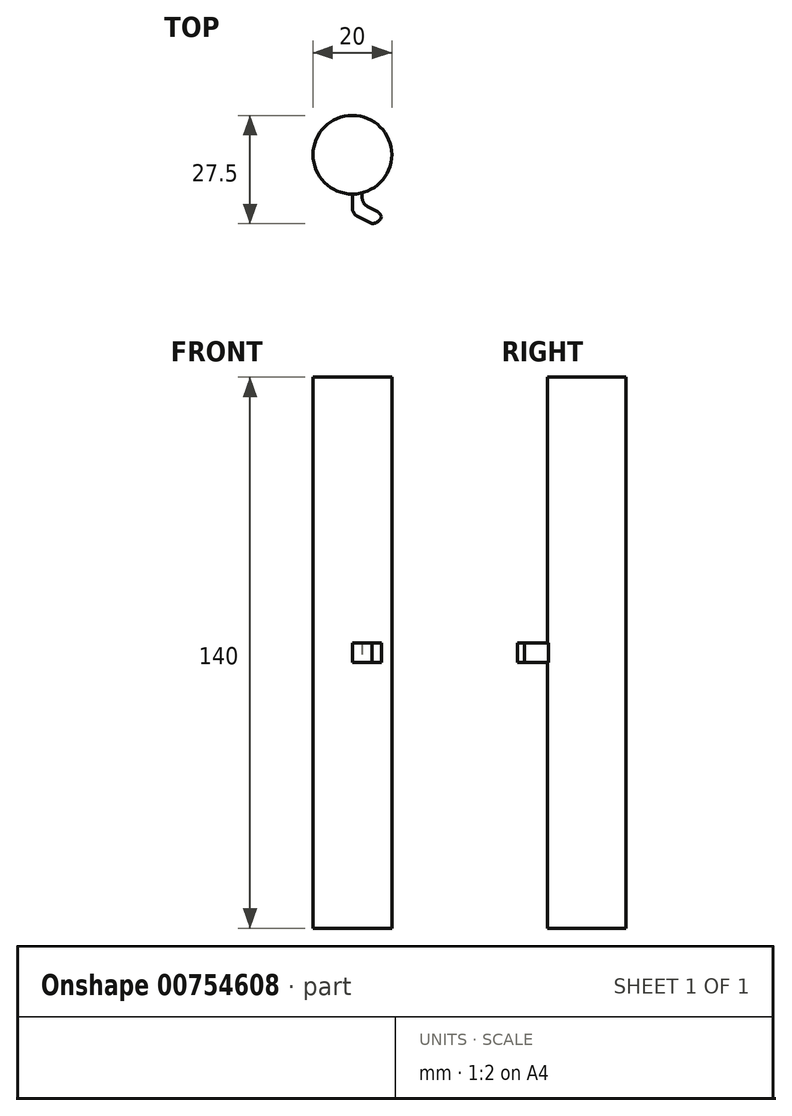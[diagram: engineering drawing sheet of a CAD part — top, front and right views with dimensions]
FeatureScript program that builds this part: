
annotation { "Feature Type Name" : "Feature", "Feature Type Description" : "" }
export const myFeature = defineFeature(function(context is Context, id is Id, definition is map)
    precondition{}
    {
        {
            var Q0;
            Q0=qCreatedBy(makeId("Top.planeOp"),FACE);
            var sketch = newSketch(context, id + "F0", { "sketchPlane" : qUnion([Q0])});
            skCircle(sketch, "E0", {"center": v(0, 0) * mm, "radius": 10 * mm});
            skLineSegment(sketch, "E1", {"start": v(0, 0) * mm, "end": v(0, -10) * mm});
            skLineSegment(sketch, "E2", {"start": v(0, -10) * mm, "end": v(0, -15) * mm});
            skLineSegment(sketch, "E3", {"start": v(0, -15) * mm, "end": v(5, -17.5) * mm});
            skLineSegment(sketch, "E4", {"start": v(5, -17.5) * mm, "end": v(7.5, -17.5) * mm});
            skLineSegment(sketch, "E5", {"start": v(7.5, -17.5) * mm, "end": v(7.5, -15) * mm});
            skLineSegment(sketch, "E6", {"start": v(7.5, -15) * mm, "end": v(2.5, -12.47) * mm});
            skLineSegment(sketch, "E7", {"start": v(2.5, -12.47) * mm, "end": v(0, -12.47) * mm});
            skLineSegment(sketch, "E8", {"start": v(2.5, -12.47) * mm, "end": v(2.5, -9.68) * mm});
            skSolve(sketch);
        }
        {
            var Q0;
            {var subQ0=sQuery(id+"F0.wireOp",EDGE,"E0");var subQ1=makeQuery(id+"F0.imprint","INTERSECT",VERTEX,{"derivedFrom":[subQ0,sQuery(id+"F0.wireOp",EDGE,"E2")]});Q0=makeQuery(id+"F0.imprint","IMPRINT",FACE,{"disambiguationData":[TD([[makeQuery(id+"F0.imprint","IMPRINT",EDGE,{"disambiguationData":[TD([[subQ1,-1.0]])],"derivedFrom":subQ0}),1.0]])]});}
            extrude(context, id + "F1", {"entities" : qUnion([Q0]), "endBound" : BoundingType.SYMMETRIC, "depth" : 140 * mm, "offsetDistance" : 25 * mm});
        }
        {
            var Q0;
            {var subQ4=sQuery(id+"F0.wireOp",EDGE,"E7");Q0=makeQuery(id+"F0.imprint","IMPRINT",FACE,{"disambiguationData":[TD([[makeQuery(id+"F0.imprint","IMPRINT",EDGE,{"derivedFrom":subQ4}),-1.0]])]});}
            var Q1;
            {var subQ0=sQuery(id+"F0.wireOp",EDGE,"E3");Q1=makeQuery(id+"F0.imprint","IMPRINT",FACE,{"disambiguationData":[TD([[makeQuery(id+"F0.imprint","IMPRINT",EDGE,{"derivedFrom":subQ0}),1.0]])]});}
            extrude(context, id + "F2", {"entities" : qUnion([Q0, Q1]), "operationType" : NewBodyOperationType.ADD, "endBound" : BoundingType.SYMMETRIC, "depth" : 5 * mm, "offsetDistance" : 25 * mm});
        }
        {
            var Q0;
            Q0=makeQuery(id+"F2.opExtrude","SWEPT_EDGE",EDGE,{"disambiguationData":[OSD([sQuery(id+"F0.wireOp",EDGE,"E5"),sQuery(id+"F0.wireOp",EDGE,"E6")])]});
            var Q1;
            Q1=makeQuery(id+"F2.opExtrude","SWEPT_EDGE",EDGE,{"disambiguationData":[OSD([sQuery(id+"F0.wireOp",EDGE,"E4"),sQuery(id+"F0.wireOp",EDGE,"E5")])]});
            var Q2;
            Q2=makeQuery(id+"F2.opExtrude","SWEPT_EDGE",EDGE,{"disambiguationData":[OSD([sQuery(id+"F0.wireOp",EDGE,"E2"),sQuery(id+"F0.wireOp",EDGE,"E3")])]});
            var Q3;
            Q3=makeQuery(id+"F2.opExtrude","SWEPT_EDGE",EDGE,{"disambiguationData":[OSD([sQuery(id+"F0.wireOp",EDGE,"E6"),sQuery(id+"F0.wireOp",EDGE,"E7"),sQuery(id+"F0.wireOp",EDGE,"E8")])]});
            fillet(context, id + "F3", {"entities" : qUnion([Q0, Q1, Q2, Q3]), "radius" : 2.5 * mm, "tangentPropagation" : true, "allowEdgeOverflow" : false});
        }
    });
